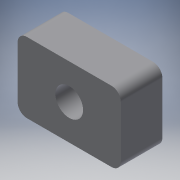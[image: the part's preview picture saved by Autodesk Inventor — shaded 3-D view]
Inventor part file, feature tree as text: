
AUTODESK INVENTOR PART (.ipt)
format: ipt  version: 2016 (Build 200138000, 138)  size: 101,888 bytes
history: native  units: in
note: dims shown in document units (in); Inventor stores cm internally (conversion verified against a paired STEP export)
features: reference x2, extrude x1, fillet x1, sketch x1
ambient origin geometry x8: Origin, YZ Plane, XZ Plane, XY Plane, X Axis, Y Axis, Z Axis, Center Point
bodies: Solid1 (feature_tree)
feature tree (5):
  extrude  "Extrusion1"  Depth=0.1772in TaperAngle=0.0deg
  fillet  "Fillet1"  Radius=0.0394in
  sketch  "Sketch1"  dims[d0=0.15in d1=0.1772in d2=0.0in d3=0.0394in]
  reference  "Reference1"
  reference  "Reference2"
